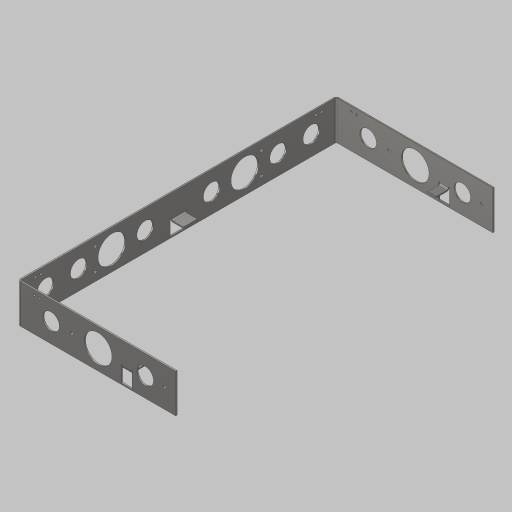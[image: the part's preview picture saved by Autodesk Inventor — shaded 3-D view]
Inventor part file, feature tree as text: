
AUTODESK INVENTOR PART (.ipt)
format: ipt  version: 2023.5 (Build 275446000, 446)  size: 438,784 bytes
history: native  units: in
note: dims shown in document units (in); Inventor stores cm internally (conversion verified against a paired STEP export)
features: sketch x13, sheet_metal_op x10, other x9, projected_geometry x7, hole x4, plane x1, mirror x1
ambient origin geometry x8: Origin, YZ Plane, XZ Plane, XY Plane, X Axis, Y Axis, Z Axis, Center Point
bodies: Solid1 (feature_tree)
feature tree (45):
  sheet_metal_op  "Face1"
  sheet_metal_op  "Flange1"
  hole  "Hole1"  [1 undecoded]
  hole  "Hole2"  [1 undecoded]
  sketch  "Sketch7"  dims[d12=0.12in]
  hole  "Hole3"  [1 undecoded]
  hole  "Hole4"  [1 undecoded]
  sheet_metal_op  "Flange2"
  sheet_metal_op  "Flange3"
  plane  "Work Plane1"
  mirror  "Mirror1"
  sketch  "Sketch1"  dims[d0=3.5in d1=28.75in]
  other  "Plate1"
  sketch  "Sketch2"  dims[d2=0.12in d3=0.12in]
  other  "Plate2"
  sheet_metal_op  "Bend1"
  sheet_metal_op  "Corner1"
  sketch  "Sketch3"  dims[d4=0.06in d5=0.24in]
  sketch  "Sketch4"  dims[d6=0.12in d7=14.25in d8=90.0deg d9=0.12in]
  sketch  "Sketch5"  dims[d10=0.48in]
  sketch  "Sketch6"  dims[d11=0.12in]
  sketch  "Sketch8"  dims[d13=2.5in]
  projected_geometry  "Projected Loop1"
  sketch  "Sketch9"  dims[d14=1.5in]
  projected_geometry  "Projected Loop2"
  sketch  "Sketch10"  dims[d15=3.0in]
  sketch  "Sketch11"  dims[d16=3.0in]
  other  "Plate3"
  sheet_metal_op  "Bend2"
  sheet_metal_op  "Corner2"
  sketch  "Sketch12"  dims[d17=3.0in]
  sketch  "Sketch13"  dims[d19=0.12in d20=0.0in d21=2.5in d22=1.5in d23=1.5in d24=4.25in d25=4.25in d26=0.12in d27=0.0in d28=2.0in d29=7.5in d30=0.25in d31=0.75in d32=0.119in d33=0.25in d34=0.5635in d35=0.12in d36=0.8108in d38=6.0in d39=0.25in d40=0.75in d41=0.375in d42=0.25in d43=0.5635in d44=1.0in d45=0.8108in d47=0.5in d49=0.438in d50=0.201in d51=0.75in d52=0.385in d53=0.25in d54=0.5635in d55=0.12in d56=0.8108in d57=0.5in d59=1.341in d60=0.438in d61=0.201in d62=0.75in d63=0.375in d64=0.25in d65=0.5635in d66=1.0in d67=0.8108in d68=1.341in d69=2.2505in d70=1.5in d71=1.125in d72=0.12in d73=0.0in d74=0.12in d75=0.06in d76=0.24in d77=0.12in d78=1.2in d79=90.0deg d80=0.12in d81=0.48in d82=0.12in d83=0.12in d84=2.2505in d85=1.125in d86=1.0in d87=0.12in d88=0.0in d89=0.12in d90=0.06in d91=0.24in d92=0.12in d93=1.2in d94=90.0deg d95=0.12in d96=0.48in d97=0.12in d98=0.12in d99=1.5in d100=3.0in d101=0.75in d102=1.25in d104=9.5936in]
  other  "Plate4"
  sheet_metal_op  "Bend3"
  sheet_metal_op  "Corner3"
  projected_geometry  "Projected Loop3"
  other  "Cut1"
  other  "Cut2"
  other  "Cut3"
  other  "Cut4"
  projected_geometry  "Project Cut Edges1"
  projected_geometry  "Project Cut Edges2"
  other  "Definition1"
  projected_geometry  "Project Cut Edges3"
  projected_geometry  "Project Cut Edges4"
note: 4 required parameter values undecoded (feature->parameter linkage not recoverable at this tier; creation-order binding heuristic only, values carry confidence <= 0.55)
